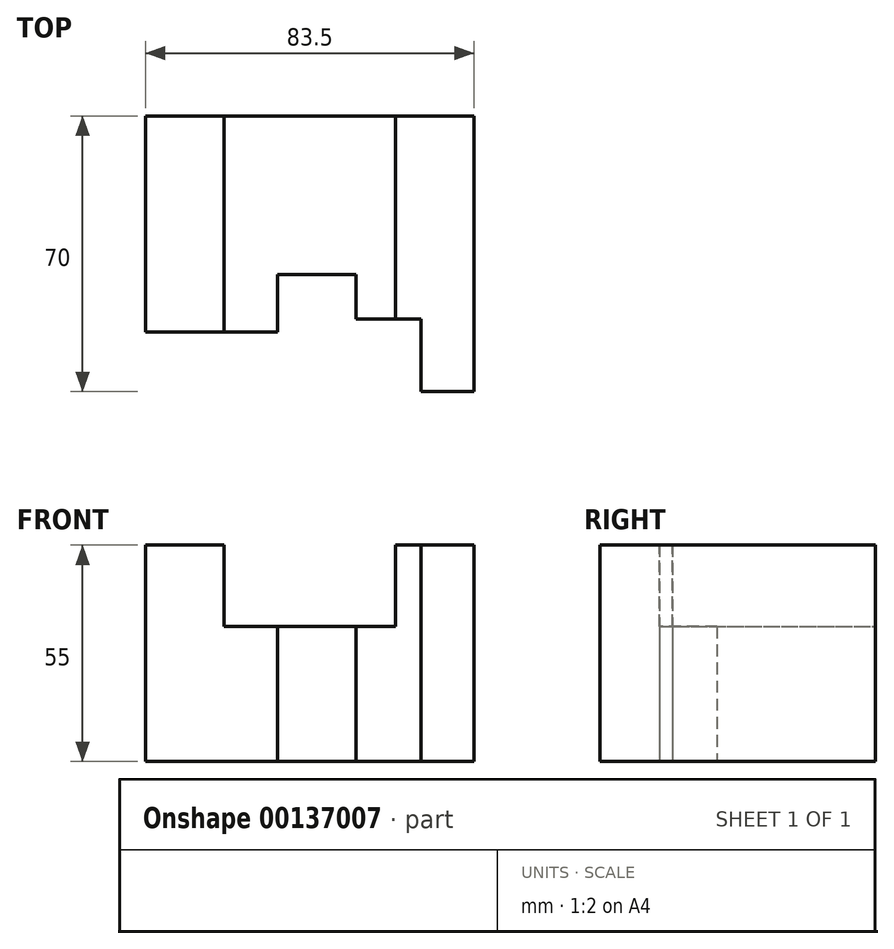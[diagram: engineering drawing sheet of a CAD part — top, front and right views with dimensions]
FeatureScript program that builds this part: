
annotation { "Feature Type Name" : "Feature", "Feature Type Description" : "" }
export const myFeature = defineFeature(function(context is Context, id is Id, definition is map)
    precondition{}
    {
        {
            var Q0;
            Q0=qCreatedBy(makeId("Front.planeOp"),FACE);
            var sketch = newSketch(context, id + "F0", { "sketchPlane" : qUnion([Q0])});
            skLineSegment(sketch, "E0.bottom", {"start": v(0, 0) * mm, "end": v(83.5, 0) * mm});
            skLineSegment(sketch, "E0.top", {"start": v(0, 55) * mm, "end": v(83.5, 55) * mm});
            skLineSegment(sketch, "E0.left", {"start": v(0, 0) * mm, "end": v(0, 55) * mm});
            skLineSegment(sketch, "E0.right", {"start": v(83.5, 0) * mm, "end": v(83.5, 55) * mm});
            skSolve(sketch);
        }
        {
            var Q0;
            Q0 = qSketchRegion(id + "F0", true);
            extrude(context, id + "F1", {"entities" : qUnion([Q0]), "depth" : 70 * mm});
        }
        {
            var Q0;
            Q0=qCreatedBy(makeId("Front.planeOp"),FACE);
            var sketch = newSketch(context, id + "F2", { "sketchPlane" : qUnion([Q0])});
            skLineSegment(sketch, "E1.bottom", {"start": v(20, 55) * mm, "end": v(63.5, 55) * mm});
            skLineSegment(sketch, "E1.top", {"start": v(20, 34.32) * mm, "end": v(63.5, 34.32) * mm});
            skLineSegment(sketch, "E1.left", {"start": v(20, 55) * mm, "end": v(20, 34.32) * mm});
            skLineSegment(sketch, "E1.right", {"start": v(63.5, 55) * mm, "end": v(63.5, 34.32) * mm});
            skSolve(sketch);
        }
        {
            var Q0;
            Q0 = qSketchRegion(id + "F2", true);
            extrude(context, id + "F3", {"entities" : qUnion([Q0]), "operationType" : NewBodyOperationType.REMOVE, "endBound" : BoundingType.THROUGH_ALL, "depth" : 25 * mm});
        }
        {
            var Q0;
            Q0=qCreatedBy(makeId("Top.planeOp"),FACE);
            var sketch = newSketch(context, id + "F4", { "sketchPlane" : qUnion([Q0])});
            skLineSegment(sketch, "E2", {"start": v(0, -54.9) * mm, "end": v(33.5, -54.9) * mm});
            skLineSegment(sketch, "E3", {"start": v(33.5, -54.9) * mm, "end": v(33.5, -40.28) * mm});
            skLineSegment(sketch, "E4", {"start": v(33.5, -40.28) * mm, "end": v(53.5, -40.28) * mm});
            skLineSegment(sketch, "E5", {"start": v(53.5, -40.28) * mm, "end": v(53.5, -51.57) * mm});
            skLineSegment(sketch, "E6", {"start": v(53.5, -51.57) * mm, "end": v(70, -51.57) * mm});
            skLineSegment(sketch, "E7", {"start": v(70, -51.57) * mm, "end": v(70, -70) * mm});
            skLineSegment(sketch, "E8", {"start": v(0, -54.9) * mm, "end": v(0, -70) * mm});
            skLineSegment(sketch, "E9", {"start": v(0, -70) * mm, "end": v(70, -70) * mm});
            skSolve(sketch);
        }
        {
            var Q0;
            Q0 = qSketchRegion(id + "F4", true);
            extrude(context, id + "F5", {"entities" : qUnion([Q0]), "operationType" : NewBodyOperationType.REMOVE, "endBound" : BoundingType.THROUGH_ALL, "depth" : 25 * mm});
        }
    });
